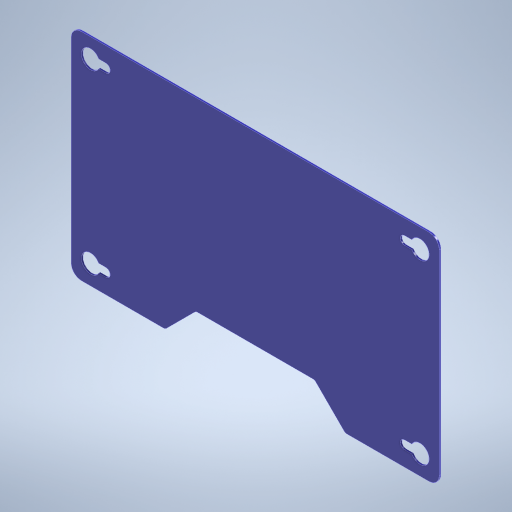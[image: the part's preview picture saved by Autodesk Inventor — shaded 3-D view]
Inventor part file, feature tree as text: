
AUTODESK INVENTOR PART (.ipt)
format: ipt  version: 2024.2 (Build 282272000, 272)  size: 354,816 bytes
history: native  units: mm
features: other x1, mirror x1
ambient origin geometry x8: Origin, YZ Plane, XZ Plane, XY Plane, X Axis, Y Axis, Z Axis, Center Point
bodies: Solid4 (feature_tree)
feature tree (2):
  other  "TorsoElectronicBoxBackFrame.ipt"
  mirror  "Mirror1"
